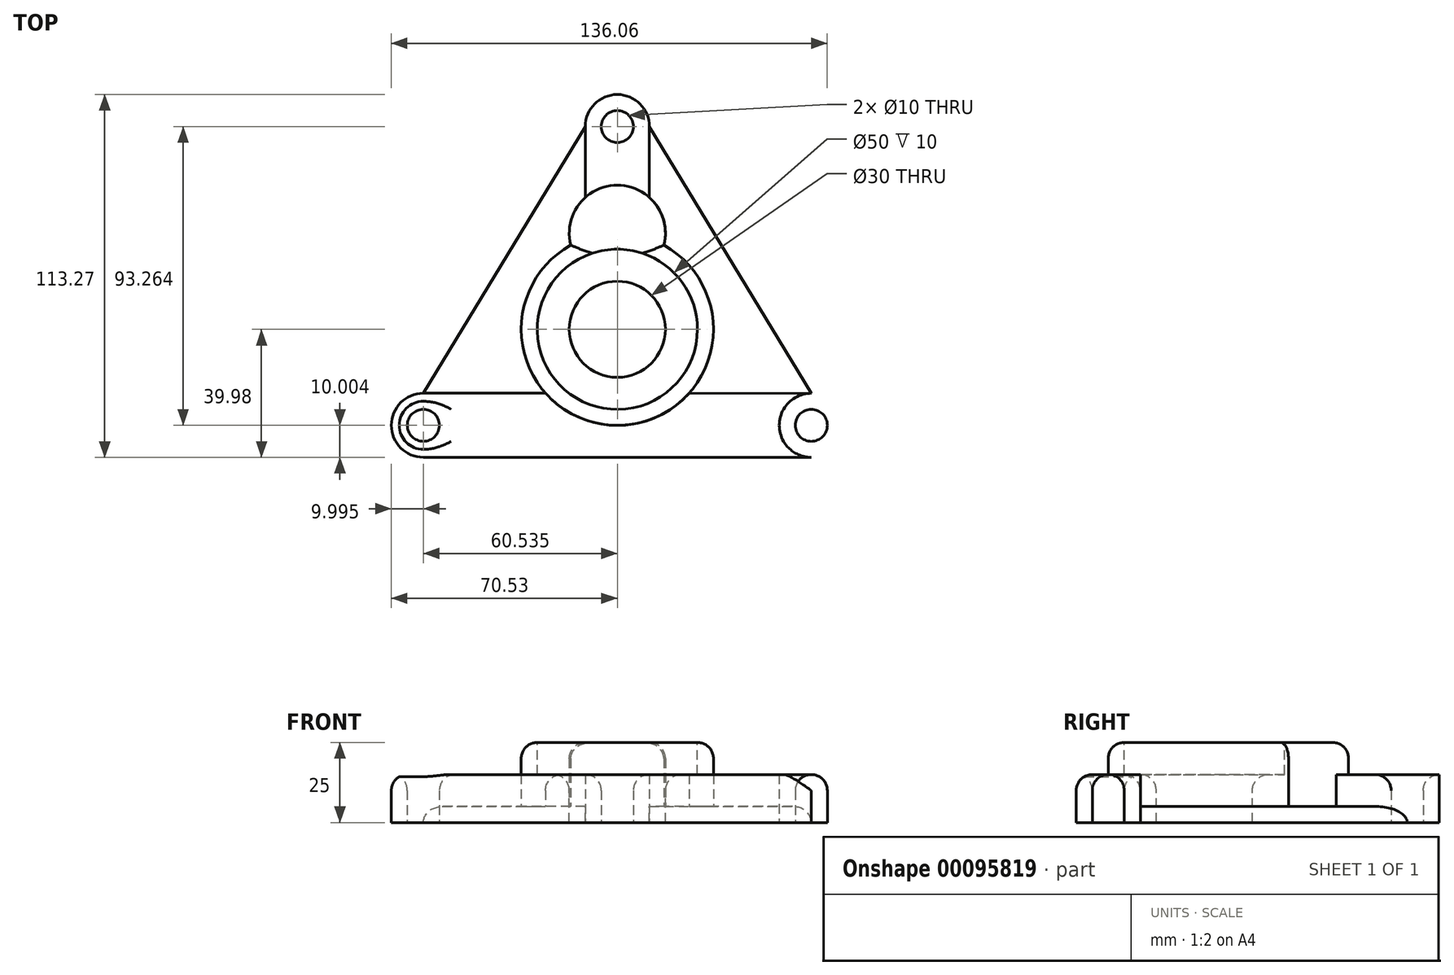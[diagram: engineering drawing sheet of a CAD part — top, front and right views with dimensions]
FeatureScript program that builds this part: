
annotation { "Feature Type Name" : "Feature", "Feature Type Description" : "" }
export const myFeature = defineFeature(function(context is Context, id is Id, definition is map)
    precondition{}
    {
        {
            var Q0;
            Q0=qCreatedBy(makeId("Top.planeOp"),FACE);
            var sketch = newSketch(context, id + "F0", { "sketchPlane" : qUnion([Q0])});
            skLineSegment(sketch, "E0", {"start": v(-69.32, 100) * mm, "end": v(-69.32, -97) * mm, "construction": true});
            skLineSegment(sketch, "E1", {"start": v(-123.55, -29.98) * mm, "end": v(84.25, -29.98) * mm, "construction": true});
            skCircle(sketch, "E2", {"center": v(0, 0) * mm, "radius": 15 * mm});
            skCircle(sketch, "E3", {"center": v(0, 0) * mm, "radius": 20 * mm});
            skCircle(sketch, "E4", {"center": v(0, 0) * mm, "radius": 25 * mm});
            skCircle(sketch, "E5", {"center": v(0, 0) * mm, "radius": 10 * mm});
            skCircle(sketch, "E6", {"center": v(0, 0) * mm, "radius": 30 * mm});
            skCircle(sketch, "E7", {"center": v(0, 30) * mm, "radius": 8 * mm});
            skCircle(sketch, "E8", {"center": v(0, 30) * mm, "radius": 10 * mm});
            skArc(sketch, "E9", {"start": v(14.52, 26.25) * mm, "mid": v(0, 45) * mm, "end": v(-14.52, 26.25) * mm});
            skCircle(sketch, "E10", {"center": v(0, 63.29) * mm, "radius": 5 * mm});
            skCircle(sketch, "E11", {"center": v(0, 63.29) * mm, "radius": 10 * mm});
            skCircle(sketch, "E12", {"center": v(-60.53, -29.98) * mm, "radius": 5 * mm});
            skCircle(sketch, "E13", {"center": v(-60.53, -29.98) * mm, "radius": 10 * mm});
            skLineSegment(sketch, "E14", {"start": v(-10, 63.29) * mm, "end": v(-10, 41.18) * mm});
            skLineSegment(sketch, "E15", {"start": v(-60.53, -19.98) * mm, "end": v(-22.38, -19.98) * mm});
            skLineSegment(sketch, "E16", {"start": v(-10, 63.29) * mm, "end": v(-60.53, -19.98) * mm});
            skLineSegment(sketch, "E17", {"start": v(0, 82.94) * mm, "end": v(0, -56.58) * mm});
            skLineSegment(sketch, "E18", {"start": v(-60.53, -39.98) * mm, "end": v(0, -39.98) * mm});
            skLineSegment(sketch, "E19.MirrorCS", {"start": v(10, 63.29) * mm, "end": v(60.53, -19.98) * mm});
            skCircle(sketch, "E20.MirrorC", {"center": v(60.53, -29.98) * mm, "radius": 10 * mm});
            skCircle(sketch, "E21.MirrorC", {"center": v(60.53, -29.98) * mm, "radius": 5 * mm});
            skLineSegment(sketch, "E22.MirrorCS", {"start": v(60.53, -39.98) * mm, "end": v(0, -39.98) * mm});
            skLineSegment(sketch, "E23", {"start": v(60.53, -19.98) * mm, "end": v(22.37, -20) * mm});
            skLineSegment(sketch, "E24", {"start": v(10, 63.29) * mm, "end": v(10, 41.18) * mm});
            skSolve(sketch);
        }
        {
            var Q0;
            {var subQ5=sQuery(id+"F0.wireOp",EDGE,"E8");var subQ7=sQuery(id+"F0.wireOp",EDGE,"E4");var subQ8=makeQuery(id+"F0.imprint","INTERSECT",VERTEX,{"disambiguationData":[OD(1.0)],"derivedFrom":[subQ7,subQ5]});Q0=makeQuery(id+"F0.imprint","IMPRINT",FACE,{"disambiguationData":[TD([[makeQuery(id+"F0.imprint","IMPRINT",EDGE,{"disambiguationData":[TD([[subQ8,-1.0]])],"derivedFrom":subQ7}),-1.0]])]});}
            var Q1;
            {var subQ3=sQuery(id+"F0.wireOp",EDGE,"E8");var subQ4=sQuery(id+"F0.wireOp",EDGE,"E4");var subQ5=makeQuery(id+"F0.imprint","INTERSECT",VERTEX,{"disambiguationData":[OD(0.0)],"derivedFrom":[subQ4,subQ3]});Q1=makeQuery(id+"F0.imprint","IMPRINT",FACE,{"disambiguationData":[TD([[makeQuery(id+"F0.imprint","IMPRINT",EDGE,{"disambiguationData":[TD([[subQ5,1.0]])],"derivedFrom":subQ4}),-1.0]])]});}
            var Q2;
            {var subQ3=sQuery(id+"F0.wireOp",EDGE,"E8");var subQ5=sQuery(id+"F0.wireOp",EDGE,"E4");var subQ6=makeQuery(id+"F0.imprint","INTERSECT",VERTEX,{"disambiguationData":[OD(0.0)],"derivedFrom":[subQ5,subQ3]});Q2=makeQuery(id+"F0.imprint","IMPRINT",FACE,{"disambiguationData":[TD([[makeQuery(id+"F0.imprint","IMPRINT",EDGE,{"disambiguationData":[TD([[subQ6,1.0]])],"derivedFrom":subQ5}),1.0]])]});}
            var Q3;
            {var subQ0=sQuery(id+"F0.wireOp",EDGE,"E17");var subQ1=sQuery(id+"F0.wireOp",EDGE,"E2");var subQ2=makeQuery(id+"F0.imprint","INTERSECT",VERTEX,{"disambiguationData":[OD(0.0)],"derivedFrom":[subQ1,subQ0]});Q3=makeQuery(id+"F0.imprint","IMPRINT",FACE,{"disambiguationData":[TD([[makeQuery(id+"F0.imprint","IMPRINT",EDGE,{"disambiguationData":[TD([[subQ2,-1.0]])],"derivedFrom":subQ1}),-1.0]])]});}
            var Q4;
            {var subQ0=sQuery(id+"F0.wireOp",EDGE,"E17");var subQ1=sQuery(id+"F0.wireOp",EDGE,"E2");var subQ2=makeQuery(id+"F0.imprint","INTERSECT",VERTEX,{"disambiguationData":[OD(0.0)],"derivedFrom":[subQ1,subQ0]});Q4=makeQuery(id+"F0.imprint","IMPRINT",FACE,{"disambiguationData":[TD([[makeQuery(id+"F0.imprint","IMPRINT",EDGE,{"disambiguationData":[TD([[subQ2,1.0]])],"derivedFrom":subQ1}),-1.0]])]});}
            var Q5;
            {var subQ0=sQuery(id+"F0.wireOp",EDGE,"E17");var subQ1=sQuery(id+"F0.wireOp",EDGE,"E2");var subQ2=makeQuery(id+"F0.imprint","INTERSECT",VERTEX,{"disambiguationData":[OD(0.0)],"derivedFrom":[subQ1,subQ0]});Q5=makeQuery(id+"F0.imprint","IMPRINT",FACE,{"disambiguationData":[TD([[makeQuery(id+"F0.imprint","IMPRINT",EDGE,{"disambiguationData":[TD([[subQ2,1.0]])],"derivedFrom":subQ1}),1.0]])]});}
            var Q6;
            {var subQ0=sQuery(id+"F0.wireOp",EDGE,"E17");var subQ1=sQuery(id+"F0.wireOp",EDGE,"E2");var subQ2=makeQuery(id+"F0.imprint","INTERSECT",VERTEX,{"disambiguationData":[OD(0.0)],"derivedFrom":[subQ1,subQ0]});Q6=makeQuery(id+"F0.imprint","IMPRINT",FACE,{"disambiguationData":[TD([[makeQuery(id+"F0.imprint","IMPRINT",EDGE,{"disambiguationData":[TD([[subQ2,-1.0]])],"derivedFrom":subQ1}),1.0]])]});}
            var Q7;
            {var subQ0=sQuery(id+"F0.wireOp",EDGE,"E17");var subQ1=sQuery(id+"F0.wireOp",EDGE,"E5");var subQ2=makeQuery(id+"F0.imprint","INTERSECT",VERTEX,{"disambiguationData":[OD(0.0)],"derivedFrom":[subQ1,subQ0]});Q7=makeQuery(id+"F0.imprint","IMPRINT",FACE,{"disambiguationData":[TD([[makeQuery(id+"F0.imprint","IMPRINT",EDGE,{"disambiguationData":[TD([[subQ2,-1.0]])],"derivedFrom":subQ1}),1.0]])]});}
            var Q8;
            {var subQ0=sQuery(id+"F0.wireOp",EDGE,"E17");var subQ1=sQuery(id+"F0.wireOp",EDGE,"E5");var subQ2=makeQuery(id+"F0.imprint","INTERSECT",VERTEX,{"disambiguationData":[OD(0.0)],"derivedFrom":[subQ1,subQ0]});Q8=makeQuery(id+"F0.imprint","IMPRINT",FACE,{"disambiguationData":[TD([[makeQuery(id+"F0.imprint","IMPRINT",EDGE,{"disambiguationData":[TD([[subQ2,1.0]])],"derivedFrom":subQ1}),1.0]])]});}
            var Q9;
            {var subQ0=sQuery(id+"F0.wireOp",EDGE,"E7");var subQ1=sQuery(id+"F0.wireOp",EDGE,"E4");var subQ2=makeQuery(id+"F0.imprint","INTERSECT",VERTEX,{"disambiguationData":[OD(0.0)],"derivedFrom":[subQ1,subQ0]});Q9=makeQuery(id+"F0.imprint","IMPRINT",FACE,{"disambiguationData":[TD([[makeQuery(id+"F0.imprint","IMPRINT",EDGE,{"disambiguationData":[TD([[subQ2,1.0]])],"derivedFrom":subQ1}),1.0]])]});}
            var Q10;
            {var subQ3=sQuery(id+"F0.wireOp",EDGE,"E8");var subQ5=sQuery(id+"F0.wireOp",EDGE,"E4");var subQ6=makeQuery(id+"F0.imprint","INTERSECT",VERTEX,{"disambiguationData":[OD(1.0)],"derivedFrom":[subQ5,subQ3]});Q10=makeQuery(id+"F0.imprint","IMPRINT",FACE,{"disambiguationData":[TD([[makeQuery(id+"F0.imprint","IMPRINT",EDGE,{"disambiguationData":[TD([[subQ6,-1.0]])],"derivedFrom":subQ5}),1.0]])]});}
            var Q11;
            {var subQ0=sQuery(id+"F0.wireOp",EDGE,"E17");var subQ1=sQuery(id+"F0.wireOp",EDGE,"E6");var subQ2=makeQuery(id+"F0.imprint","INTERSECT",VERTEX,{"disambiguationData":[OD(0.0)],"derivedFrom":[subQ1,subQ0]});Q11=makeQuery(id+"F0.imprint","IMPRINT",FACE,{"disambiguationData":[TD([[makeQuery(id+"F0.imprint","IMPRINT",EDGE,{"disambiguationData":[TD([[subQ2,-1.0]])],"derivedFrom":subQ1}),-1.0]])]});}
            var Q12;
            {var subQ0=sQuery(id+"F0.wireOp",EDGE,"E7");var subQ1=sQuery(id+"F0.wireOp",EDGE,"E6");var subQ2=makeQuery(id+"F0.imprint","INTERSECT",VERTEX,{"disambiguationData":[OD(0.0)],"derivedFrom":[subQ1,subQ0]});Q12=makeQuery(id+"F0.imprint","IMPRINT",FACE,{"disambiguationData":[TD([[makeQuery(id+"F0.imprint","IMPRINT",EDGE,{"disambiguationData":[TD([[subQ2,-1.0]])],"derivedFrom":subQ1}),-1.0]])]});}
            var Q13;
            {var subQ0=sQuery(id+"F0.wireOp",EDGE,"E8");var subQ1=sQuery(id+"F0.wireOp",EDGE,"E6");var subQ2=makeQuery(id+"F0.imprint","INTERSECT",VERTEX,{"disambiguationData":[OD(0.0)],"derivedFrom":[subQ1,subQ0]});Q13=makeQuery(id+"F0.imprint","IMPRINT",FACE,{"disambiguationData":[TD([[makeQuery(id+"F0.imprint","IMPRINT",EDGE,{"disambiguationData":[TD([[subQ2,-1.0]])],"derivedFrom":subQ1}),-1.0]])]});}
            var Q14;
            {var subQ0=sQuery(id+"F0.wireOp",EDGE,"E9");var subQ4=sQuery(id+"F0.wireOp",EDGE,"E6");var subQ5=makeQuery(id+"F0.imprint","INTERSECT",VERTEX,{"disambiguationData":[OD(0.0)],"derivedFrom":[subQ4,subQ0]});Q14=makeQuery(id+"F0.imprint","IMPRINT",FACE,{"disambiguationData":[TD([[makeQuery(id+"F0.imprint","IMPRINT",EDGE,{"disambiguationData":[TD([[subQ5,-1.0]])],"derivedFrom":subQ4}),-1.0]])]});}
            var Q15;
            {var subQ0=sQuery(id+"F0.wireOp",EDGE,"E9");var subQ1=sQuery(id+"F0.wireOp",EDGE,"E6");var subQ2=makeQuery(id+"F0.imprint","INTERSECT",VERTEX,{"disambiguationData":[OD(1.0)],"derivedFrom":[subQ1,subQ0]});Q15=makeQuery(id+"F0.imprint","IMPRINT",FACE,{"disambiguationData":[TD([[makeQuery(id+"F0.imprint","IMPRINT",EDGE,{"disambiguationData":[TD([[subQ2,1.0]])],"derivedFrom":subQ1}),-1.0]])]});}
            var Q16;
            {var subQ0=sQuery(id+"F0.wireOp",EDGE,"E7");var subQ1=sQuery(id+"F0.wireOp",EDGE,"E6");var subQ2=makeQuery(id+"F0.imprint","INTERSECT",VERTEX,{"disambiguationData":[OD(1.0)],"derivedFrom":[subQ1,subQ0]});Q16=makeQuery(id+"F0.imprint","IMPRINT",FACE,{"disambiguationData":[TD([[makeQuery(id+"F0.imprint","IMPRINT",EDGE,{"disambiguationData":[TD([[subQ2,-1.0]])],"derivedFrom":subQ1}),-1.0]])]});}
            var Q17;
            {var subQ0=sQuery(id+"F0.wireOp",EDGE,"E17");var subQ1=sQuery(id+"F0.wireOp",EDGE,"E4");var subQ2=makeQuery(id+"F0.imprint","INTERSECT",VERTEX,{"disambiguationData":[OD(0.0)],"derivedFrom":[subQ1,subQ0]});Q17=makeQuery(id+"F0.imprint","IMPRINT",FACE,{"disambiguationData":[TD([[makeQuery(id+"F0.imprint","IMPRINT",EDGE,{"disambiguationData":[TD([[subQ2,-1.0]])],"derivedFrom":subQ1}),-1.0]])]});}
            var Q18;
            {var subQ0=sQuery(id+"F0.wireOp",EDGE,"E7");var subQ1=sQuery(id+"F0.wireOp",EDGE,"E4");var subQ2=makeQuery(id+"F0.imprint","INTERSECT",VERTEX,{"disambiguationData":[OD(0.0)],"derivedFrom":[subQ1,subQ0]});Q18=makeQuery(id+"F0.imprint","IMPRINT",FACE,{"disambiguationData":[TD([[makeQuery(id+"F0.imprint","IMPRINT",EDGE,{"disambiguationData":[TD([[subQ2,-1.0]])],"derivedFrom":subQ1}),-1.0]])]});}
            var Q19;
            {var subQ0=sQuery(id+"F0.wireOp",EDGE,"E7");var subQ1=sQuery(id+"F0.wireOp",EDGE,"E4");var subQ2=makeQuery(id+"F0.imprint","INTERSECT",VERTEX,{"disambiguationData":[OD(1.0)],"derivedFrom":[subQ1,subQ0]});Q19=makeQuery(id+"F0.imprint","IMPRINT",FACE,{"disambiguationData":[TD([[makeQuery(id+"F0.imprint","IMPRINT",EDGE,{"disambiguationData":[TD([[subQ2,-1.0]])],"derivedFrom":subQ1}),1.0]])]});}
            var Q20;
            {var subQ0=sQuery(id+"F0.wireOp",EDGE,"E7");var subQ1=sQuery(id+"F0.wireOp",EDGE,"E4");var subQ2=makeQuery(id+"F0.imprint","INTERSECT",VERTEX,{"disambiguationData":[OD(0.0)],"derivedFrom":[subQ1,subQ0]});Q20=makeQuery(id+"F0.imprint","IMPRINT",FACE,{"disambiguationData":[TD([[makeQuery(id+"F0.imprint","IMPRINT",EDGE,{"disambiguationData":[TD([[subQ2,-1.0]])],"derivedFrom":subQ1}),1.0]])]});}
            var Q21;
            {var subQ0=sQuery(id+"F0.wireOp",EDGE,"E17");var subQ1=sQuery(id+"F0.wireOp",EDGE,"E4");var subQ2=makeQuery(id+"F0.imprint","INTERSECT",VERTEX,{"disambiguationData":[OD(0.0)],"derivedFrom":[subQ1,subQ0]});Q21=makeQuery(id+"F0.imprint","IMPRINT",FACE,{"disambiguationData":[TD([[makeQuery(id+"F0.imprint","IMPRINT",EDGE,{"disambiguationData":[TD([[subQ2,-1.0]])],"derivedFrom":subQ1}),1.0]])]});}
            var Q22;
            {var subQ0=sQuery(id+"F0.wireOp",EDGE,"E7");var subQ1=sQuery(id+"F0.wireOp",EDGE,"E4");var subQ2=makeQuery(id+"F0.imprint","INTERSECT",VERTEX,{"disambiguationData":[OD(1.0)],"derivedFrom":[subQ1,subQ0]});Q22=makeQuery(id+"F0.imprint","IMPRINT",FACE,{"disambiguationData":[TD([[makeQuery(id+"F0.imprint","IMPRINT",EDGE,{"disambiguationData":[TD([[subQ2,-1.0]])],"derivedFrom":subQ1}),-1.0]])]});}
            var Q23;
            {var subQ0=sQuery(id+"F0.wireOp",EDGE,"E7");var subQ1=sQuery(id+"F0.wireOp",EDGE,"E4");var subQ2=makeQuery(id+"F0.imprint","INTERSECT",VERTEX,{"disambiguationData":[OD(0.0)],"derivedFrom":[subQ1,subQ0]});Q23=makeQuery(id+"F0.imprint","IMPRINT",FACE,{"disambiguationData":[TD([[makeQuery(id+"F0.imprint","IMPRINT",EDGE,{"disambiguationData":[TD([[subQ2,1.0]])],"derivedFrom":subQ1}),-1.0]])]});}
            extrude(context, id + "F1", {"entities" : qUnion([Q0, Q1, Q2, Q3, Q4, Q5, Q6, Q7, Q8, Q9, Q10, Q11, Q12, Q13, Q14, Q15, Q16, Q17, Q18, Q19, Q20, Q21, Q22, Q23]), "depth" : 25 * mm});
        }
        {
            var Q0;
            {var subQ0=sQuery(id+"F0.wireOp",EDGE,"E15");Q0=makeQuery(id+"F0.imprint","IMPRINT",FACE,{"disambiguationData":[TD([[makeQuery(id+"F0.imprint","IMPRINT",EDGE,{"derivedFrom":subQ0}),-1.0]])]});}
            var Q1;
            {var subQ0=sQuery(id+"F0.wireOp",EDGE,"E22.MirrorCS");Q1=makeQuery(id+"F0.imprint","IMPRINT",FACE,{"disambiguationData":[TD([[makeQuery(id+"F0.imprint","IMPRINT",EDGE,{"derivedFrom":subQ0}),-1.0]])]});}
            var Q2;
            Q2=makeQuery(id+"F0.imprint","IMPRINT",FACE,{"disambiguationData":[TD([[makeQuery(id+"F0.imprint","IMPRINT",EDGE,{"derivedFrom":sQuery(id+"F0.wireOp",EDGE,"E21.MirrorC")}),1.0]])]});
            var Q3;
            Q3=makeQuery(id+"F0.imprint","IMPRINT",FACE,{"disambiguationData":[TD([[makeQuery(id+"F0.imprint","IMPRINT",EDGE,{"derivedFrom":sQuery(id+"F0.wireOp",EDGE,"E12")}),-1.0]])]});
            var Q4;
            {var subQ0=sQuery(id+"F0.wireOp",EDGE,"E14");Q4=makeQuery(id+"F0.imprint","IMPRINT",FACE,{"disambiguationData":[TD([[makeQuery(id+"F0.imprint","IMPRINT",EDGE,{"derivedFrom":subQ0}),1.0]])]});}
            var Q5;
            {var subQ0=sQuery(id+"F0.wireOp",EDGE,"E24");Q5=makeQuery(id+"F0.imprint","IMPRINT",FACE,{"disambiguationData":[TD([[makeQuery(id+"F0.imprint","IMPRINT",EDGE,{"derivedFrom":subQ0}),-1.0]])]});}
            var Q6;
            {var subQ0=sQuery(id+"F0.wireOp",EDGE,"E17");var subQ3=sQuery(id+"F0.wireOp",EDGE,"E10");var subQ4=makeQuery(id+"F0.imprint","INTERSECT",VERTEX,{"disambiguationData":[OD(0.0)],"derivedFrom":[subQ3,subQ0]});Q6=makeQuery(id+"F0.imprint","IMPRINT",FACE,{"disambiguationData":[TD([[makeQuery(id+"F0.imprint","IMPRINT",EDGE,{"disambiguationData":[TD([[subQ4,1.0]])],"derivedFrom":subQ3}),-1.0]])]});}
            var Q7;
            {var subQ0=sQuery(id+"F0.wireOp",EDGE,"E17");var subQ3=sQuery(id+"F0.wireOp",EDGE,"E10");var subQ4=makeQuery(id+"F0.imprint","INTERSECT",VERTEX,{"disambiguationData":[OD(0.0)],"derivedFrom":[subQ3,subQ0]});Q7=makeQuery(id+"F0.imprint","IMPRINT",FACE,{"disambiguationData":[TD([[makeQuery(id+"F0.imprint","IMPRINT",EDGE,{"disambiguationData":[TD([[subQ4,-1.0]])],"derivedFrom":subQ3}),-1.0]])]});}
            extrude(context, id + "F2", {"entities" : qUnion([Q0, Q1, Q2, Q3, Q4, Q5, Q6, Q7]), "operationType" : NewBodyOperationType.ADD, "depth" : 15 * mm});
        }
        {
            var Q0;
            {var subQ0=sQuery(id+"F0.wireOp",EDGE,"E14");Q0=makeQuery(id+"F0.imprint","IMPRINT",FACE,{"disambiguationData":[TD([[makeQuery(id+"F0.imprint","IMPRINT",EDGE,{"derivedFrom":subQ0}),-1.0]])]});}
            var Q1;
            {var subQ1=sQuery(id+"F0.wireOp",EDGE,"E19.MirrorCS");Q1=makeQuery(id+"F0.imprint","IMPRINT",FACE,{"disambiguationData":[TD([[makeQuery(id+"F0.imprint","IMPRINT",EDGE,{"derivedFrom":subQ1}),-1.0]])]});}
            extrude(context, id + "F3", {"entities" : qUnion([Q0, Q1]), "operationType" : NewBodyOperationType.ADD, "depth" : 5 * mm});
        }
        {
            var Q0;
            Q0=makeQuery(id+"F1.opExtrude","CAP_FACE",FACE,{"disambiguationData":[OSD([sQuery(id+"F0.wireOp",EDGE,"E6"),sQuery(id+"F0.wireOp",EDGE,"E9")])],"isStart":false});
            var sketch = newSketch(context, id + "F4", { "sketchPlane" : qUnion([Q0])});
            skCircle(sketch, "E25.0", {"center": v(0, 0) * mm, "radius": 25 * mm});
            skSolve(sketch);
        }
        {
            var Q0;
            Q0 = qSketchRegion(id + "F4", true);
            extrude(context, id + "F5", {"entities" : qUnion([Q0]), "operationType" : NewBodyOperationType.REMOVE, "oppositeDirection" : true, "depth" : 10 * mm});
        }
        {
            var Q0;
            Q0=makeQuery(id+"F4.imprint","IMPRINT",FACE,{"disambiguationData":[TD([[makeQuery(id+"F4.imprint","IMPRINT",EDGE,{"derivedFrom":sQuery(id+"F4.wireOp",EDGE,"E25.0")}),1.0]])]});
            var sketch = newSketch(context, id + "F6", { "sketchPlane" : qUnion([Q0])});
            skCircle(sketch, "E26.0", {"center": v(0, 0) * mm, "radius": 15 * mm});
            skSolve(sketch);
        }
        {
            var Q0;
            Q0 = qSketchRegion(id + "F6", true);
            extrude(context, id + "F7", {"entities" : qUnion([Q0]), "operationType" : NewBodyOperationType.REMOVE, "oppositeDirection" : true, "depth" : 25 * mm});
        }
        {
            var Q0;
            Q0=makeQuery(id+"F2.opExtrude","CAP_EDGE",EDGE,{"disambiguationData":[OSD([sQuery(id+"F0.wireOp",EDGE,"E12")])],"isStart":false});
            var Q1;
            Q1=makeQuery(id+"F2.opExtrude","CAP_EDGE",EDGE,{"disambiguationData":[OSD([sQuery(id+"F0.wireOp",EDGE,"E10")])],"isStart":false});
            var Q2;
            Q2=makeQuery(id+"F2.opExtrude","CAP_EDGE",EDGE,{"disambiguationData":[OSD([sQuery(id+"F0.wireOp",EDGE,"E21.MirrorC")])],"isStart":false});
            var Q3;
            Q3=makeQuery(id+"F5.boolean.opBoolean","COPY",EDGE,{"derivedFrom":makeQuery(id+"F5.opExtrude","CAP_EDGE",EDGE,{"disambiguationData":[OSD([sQuery(id+"F4.wireOp",EDGE,"E25.0")])],"isStart":true})});
            var Q4;
            Q4=makeQuery(id+"F7.boolean.opBoolean","INTERSECT",EDGE,{"derivedFrom":[makeQuery(id+"F5.boolean.opBoolean","COPY",FACE,{"derivedFrom":makeQuery(id+"F5.opExtrude","CAP_FACE",FACE,{"disambiguationData":[OSD([sQuery(id+"F4.wireOp",EDGE,"E25.0")])],"isStart":false})}),makeQuery(id+"F7.opExtrude","SWEPT_FACE",FACE,{"disambiguationData":[OSD([sQuery(id+"F6.wireOp",EDGE,"E26.0")])]})]});
            var Q5;
            Q5=makeQuery(id+"F1.opExtrude","CAP_EDGE",EDGE,{"disambiguationData":[OSD([sQuery(id+"F0.wireOp",EDGE,"E9")])],"isStart":false});
            var Q6;
            Q6=makeQuery(id+"F1.opExtrude","CAP_EDGE",EDGE,{"disambiguationData":[OSD([sQuery(id+"F0.wireOp",EDGE,"E6")])],"isStart":false});
            var Q7;
            Q7=makeQuery(id+"F2.opExtrude","CAP_EDGE",EDGE,{"disambiguationData":[OSD([sQuery(id+"F0.wireOp",EDGE,"E18"),sQuery(id+"F0.wireOp",EDGE,"E22.MirrorCS")])],"isStart":false});
            var Q8;
            Q8=makeQuery(id+"F3.opExtrude","CAP_EDGE",EDGE,{"disambiguationData":[OSD([sQuery(id+"F0.wireOp",EDGE,"E19.MirrorCS")])],"isStart":false});
            var Q9;
            Q9=makeQuery(id+"F3.opExtrude","CAP_EDGE",EDGE,{"disambiguationData":[OSD([sQuery(id+"F0.wireOp",EDGE,"E16")])],"isStart":false});
            fillet(context, id + "F8", {"entities" : qUnion([Q0, Q1, Q2, Q3, Q4, Q5, Q6, Q7, Q8, Q9]), "radius" : 5 * mm, "tangentPropagation" : true, "allowEdgeOverflow" : false});
        }
    });
